# Revit family: Mixer tap-Deck_mounted-PRESTO-NEO DUO S 15SEC-64701
name_source: partatom
category: Plumbing Fixtures
revit_build: Autodesk Revit 2014 (Build: 20130308_1515(x64)
units: mm (PartAtom-declared; Revit-internal decimal feet)

## types (1)
- 64701
    CW Inlet = 13 mm
    Default Elevation = 1219 mm
    Description = PRESTO NEO DUO S Single deck-mounted tap
    Drain Connection = 0 mm  [stored 0 ft]
    Edition number = 1
    Flow (at 3 bar - 4-position flow adjustment device) = 0.1 L/s
    HW Inlet = 13 mm
    Height = 133 mm  [stored 0.436352 ft]
    Manufacturer = PRESTO LES ROBINETS
    Manufacturer name = Presto
    Material main = Brass
    Material secondary = Chrome
    Model = 64701
    Nominal height = 10000
    Nominal width = 13300
    Operating Pressure = 1 to 5 bar
    Outlet = 0 mm  [stored 0 ft]
    Primary Material = Brass-Presto
    Product Guid = 28a92778-90da-4837-b544-f0ae950b5235
    Product SKU = 64700
    Product data url = http://bimobject.com
    Product family = NEO DUO
    Product group = ROBINET
    QR code = http://bimobject.com
    Secondary Material = Chrome-Presto
    Temp - Resistance(30 minute Thermal Shock) = 75 °C
    Time Flow (± 5 sec) = 15.0 s
    Warranty = 10
    Weight Net (Kg) = 0
    Width = 100 mm  [stored 0.328084 ft]

note: [stored X ft] marks values corroborated as IEEE doubles in the binary element streams (Revit-internal decimal feet)

## geometry (parser evidence)
native form markers: Sweep x8
no freeform markers — native parametric forms only
